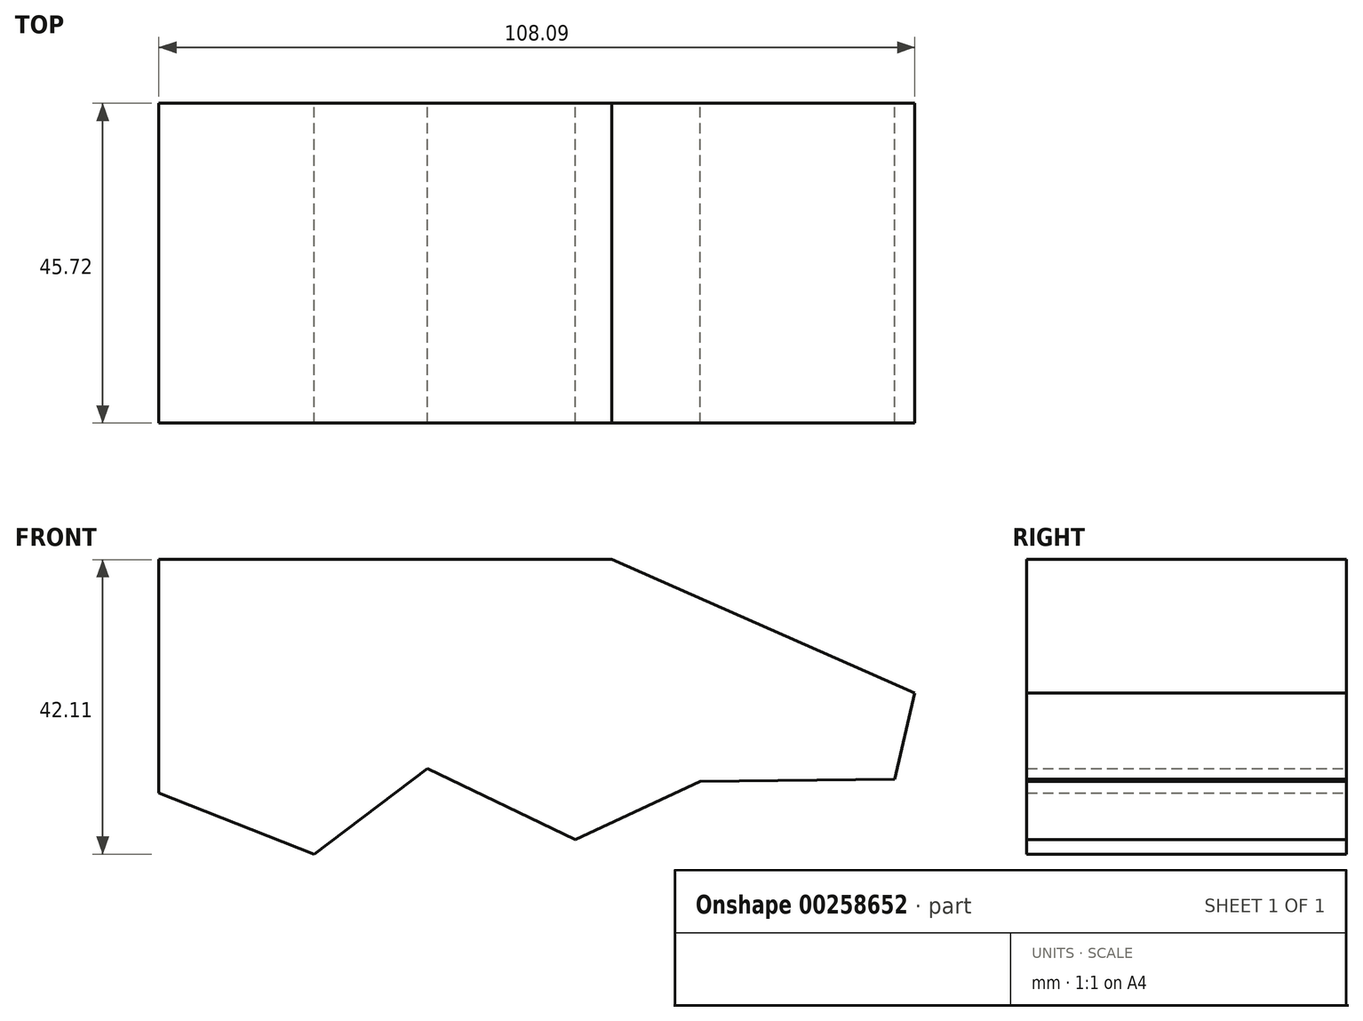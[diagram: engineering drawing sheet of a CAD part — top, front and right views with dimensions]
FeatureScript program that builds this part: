
annotation { "Feature Type Name" : "Feature", "Feature Type Description" : "" }
export const myFeature = defineFeature(function(context is Context, id is Id, definition is map)
    precondition{}
    {
        {
            var Q0;
            Q0=qCreatedBy(makeId("Front.planeOp"),FACE);
            var sketch = newSketch(context, id + "F0", { "sketchPlane" : qUnion([Q0])});
            skLineSegment(sketch, "E0", {"start": v(60.58, 30.5) * mm, "end": v(17.22, 49.58) * mm});
            skLineSegment(sketch, "E1", {"start": v(17.22, 49.58) * mm, "end": v(-47.5, 49.58) * mm});
            skLineSegment(sketch, "E2", {"start": v(-47.5, 49.58) * mm, "end": v(-47.5, 29.25) * mm});
            skLineSegment(sketch, "E3", {"start": v(-47.5, 16.18) * mm, "end": v(-47.5, 29.25) * mm});
            skPoint(sketch, "E3.startSnap0", {"position": v(-47.5, 39.42) * mm});
            skLineSegment(sketch, "E4", {"start": v(-47.5, 16.18) * mm, "end": v(-25.3, 7.47) * mm});
            skLineSegment(sketch, "E5", {"start": v(-25.3, 7.47) * mm, "end": v(-9.13, 19.7) * mm});
            skLineSegment(sketch, "E6", {"start": v(-9.13, 19.7) * mm, "end": v(12.03, 9.54) * mm});
            skLineSegment(sketch, "E7", {"start": v(12.03, 9.54) * mm, "end": v(29.87, 17.84) * mm});
            skLineSegment(sketch, "E8", {"start": v(29.87, 17.84) * mm, "end": v(57.67, 18.16) * mm});
            skLineSegment(sketch, "E9", {"start": v(57.67, 18.16) * mm, "end": v(60.58, 30.5) * mm});
            skSolve(sketch);
        }
        {
            var Q0;
            Q0 = qSketchRegion(id + "F0", true);
            var Q1;
            Q1=makeQuery(id+"F0.imprint","IMPRINT",FACE,{"disambiguationData":[TD([[makeQuery(id+"F0.imprint","IMPRINT",EDGE,{"derivedFrom":sQuery(id+"F0.wireOp",EDGE,"E0")}),1.0]])]});
            extrude(context, id + "F1", {"entities" : qUnion([Q0, Q1]), "depth" : 45.72 * mm});
        }
    });
